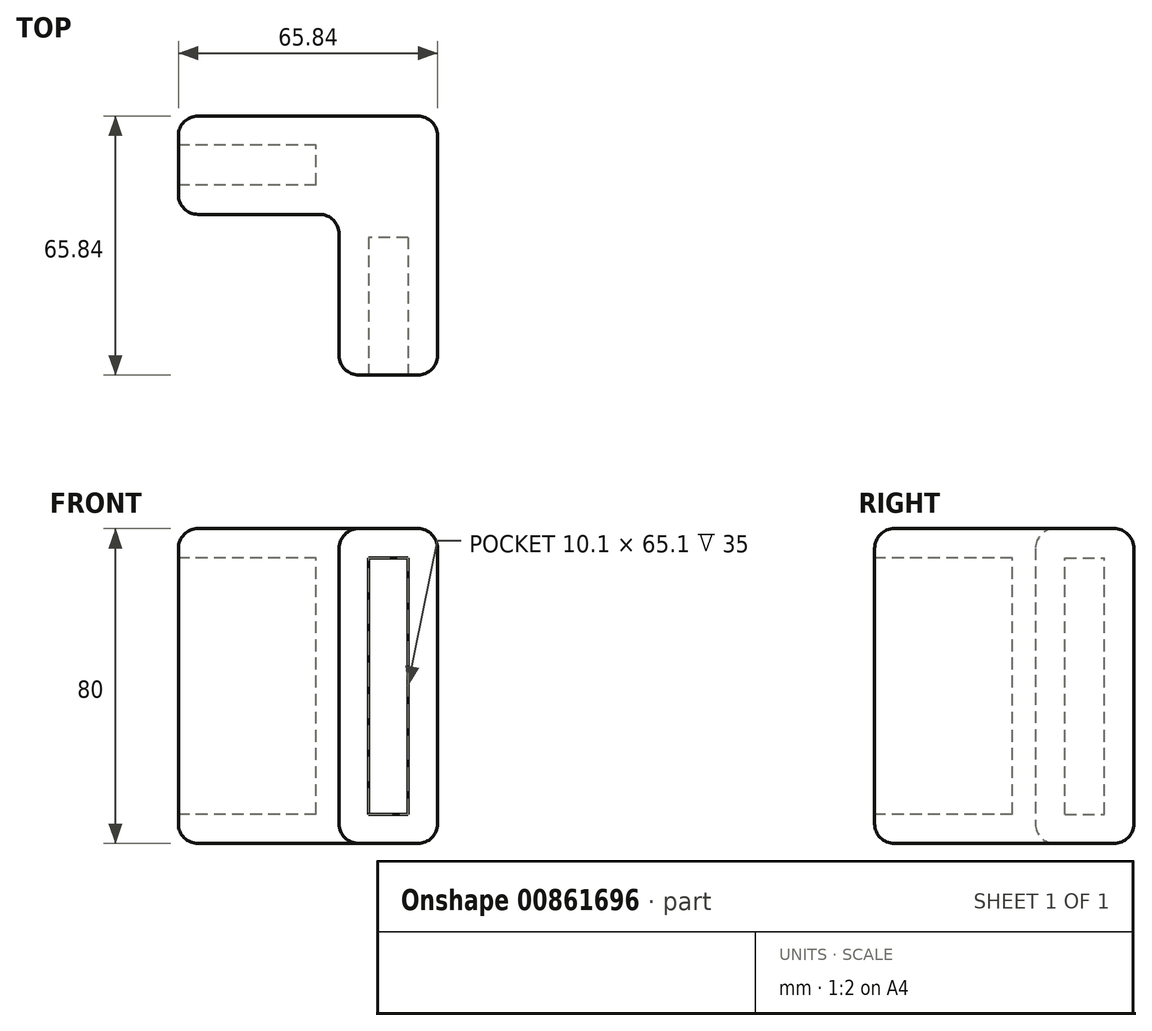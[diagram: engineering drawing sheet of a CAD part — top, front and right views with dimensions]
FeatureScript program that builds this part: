
annotation { "Feature Type Name" : "Feature", "Feature Type Description" : "" }
export const myFeature = defineFeature(function(context is Context, id is Id, definition is map)
    precondition{}
    {
        {
            var Q0;
            Q0=qCreatedBy(makeId("Top.planeOp"),FACE);
            var sketch = newSketch(context, id + "F0", { "sketchPlane" : qUnion([Q0])});
            skLineSegment(sketch, "E0", {"start": v(0, 0) * mm, "end": v(35.84, 0) * mm});
            skLineSegment(sketch, "E1", {"start": v(40.84, -5) * mm, "end": v(40.84, -40.84) * mm});
            skLineSegment(sketch, "E2", {"start": v(40.84, -40.84) * mm, "end": v(48.29, -40.84) * mm});
            skLineSegment(sketch, "E3", {"start": v(48.29, -40.84) * mm, "end": v(48.29, -5.84) * mm});
            skLineSegment(sketch, "E4", {"start": v(48.29, -5.84) * mm, "end": v(58.39, -5.84) * mm});
            skLineSegment(sketch, "E5", {"start": v(58.39, -5.84) * mm, "end": v(58.39, -40.84) * mm});
            skLineSegment(sketch, "E6", {"start": v(58.39, -40.84) * mm, "end": v(65.84, -40.84) * mm});
            skLineSegment(sketch, "E7", {"start": v(65.84, -40.84) * mm, "end": v(65.84, 20) * mm});
            skLineSegment(sketch, "E8", {"start": v(60.84, 25) * mm, "end": v(0, 25) * mm});
            skLineSegment(sketch, "E9", {"start": v(0, 25) * mm, "end": v(0, 17.55) * mm});
            skLineSegment(sketch, "E10", {"start": v(0, 17.55) * mm, "end": v(35, 17.55) * mm});
            skLineSegment(sketch, "E11", {"start": v(35, 17.55) * mm, "end": v(35, 7.45) * mm});
            skLineSegment(sketch, "E12", {"start": v(35, 7.45) * mm, "end": v(0, 7.45) * mm});
            skLineSegment(sketch, "E13", {"start": v(0, 7.45) * mm, "end": v(0, 0) * mm});
            skPoint(sketch, "E14.visualSharp", {"position": v(65.84, 25) * mm});
            skArc(sketch, "E14.filletArc", {"start": v(65.84, 20) * mm, "mid": v(64.37, 23.54) * mm, "end": v(60.84, 25) * mm});
            skPoint(sketch, "E15.visualSharp", {"position": v(40.84, 0) * mm});
            skArc(sketch, "E15.filletArc", {"start": v(40.84, -5) * mm, "mid": v(39.37, -1.46) * mm, "end": v(35.84, 0) * mm});
            skLineSegment(sketch, "E16", {"start": v(48.29, -40.84) * mm, "end": v(58.39, -40.84) * mm});
            skLineSegment(sketch, "E17", {"start": v(0, 17.55) * mm, "end": v(0, 7.45) * mm});
            skSolve(sketch);
        }
        {
            var Q0;
            Q0=makeQuery(id+"F0.imprint","IMPRINT",FACE,{"disambiguationData":[TD([[makeQuery(id+"F0.imprint","IMPRINT",EDGE,{"derivedFrom":sQuery(id+"F0.wireOp",EDGE,"E0")}),1.0]])]});
            var Q1;
            Q1=makeQuery(id+"F0.imprint","IMPRINT",FACE,{"disambiguationData":[TD([[makeQuery(id+"F0.imprint","IMPRINT",EDGE,{"derivedFrom":sQuery(id+"F0.wireOp",EDGE,"E10")}),-1.0]])]});
            var Q2;
            Q2=makeQuery(id+"F0.imprint","IMPRINT",FACE,{"disambiguationData":[TD([[makeQuery(id+"F0.imprint","IMPRINT",EDGE,{"derivedFrom":sQuery(id+"F0.wireOp",EDGE,"E3")}),-1.0]])]});
            extrude(context, id + "F1", {"entities" : qUnion([Q0, Q1, Q2]), "depth" : 80 * mm, "offsetDistance" : 25 * mm});
        }
        {
            var Q0;
            Q0=makeQuery(id+"F1.opExtrude","SWEPT_FACE",FACE,{"disambiguationData":[OSD([sQuery(id+"F0.wireOp",EDGE,"E9"),sQuery(id+"F0.wireOp",EDGE,"E13"),sQuery(id+"F0.wireOp",EDGE,"E17")])]});
            var sketch = newSketch(context, id + "F2", { "sketchPlane" : qUnion([Q0])});
            skLineSegment(sketch, "E18.0", {"start": v(-25, 80) * mm, "end": v(-25, 0) * mm});
            skPoint(sketch, "E19.0", {"position": v(-12.5, 80) * mm});
            skPoint(sketch, "E20.0", {"position": v(0, 40) * mm});
            skPoint(sketch, "E21.0", {"position": v(-12.5, 0) * mm});
            skLineSegment(sketch, "E22.bottom", {"start": v(-7.45, 7.45) * mm, "end": v(-17.55, 7.45) * mm});
            skLineSegment(sketch, "E22.top", {"start": v(-7.45, 72.55) * mm, "end": v(-17.55, 72.55) * mm});
            skLineSegment(sketch, "E22.left", {"start": v(-7.45, 7.45) * mm, "end": v(-7.45, 72.55) * mm});
            skLineSegment(sketch, "E22.right", {"start": v(-17.55, 7.45) * mm, "end": v(-17.55, 72.55) * mm});
            skPoint(sketch, "E22.middle", {"position": v(-12.5, 40) * mm});
            skSolve(sketch);
        }
        {
            var Q0;
            Q0=makeQuery(id+"F1.opExtrude","SWEPT_FACE",FACE,{"disambiguationData":[OSD([sQuery(id+"F0.wireOp",EDGE,"E2"),sQuery(id+"F0.wireOp",EDGE,"E6"),sQuery(id+"F0.wireOp",EDGE,"E16")])]});
            var sketch = newSketch(context, id + "F3", { "sketchPlane" : qUnion([Q0])});
            skLineSegment(sketch, "E23.0.0", {"start": v(40.84, 0) * mm, "end": v(65.84, 0) * mm});
            skLineSegment(sketch, "E23.0.1", {"start": v(65.84, 0) * mm, "end": v(65.84, 80) * mm});
            skLineSegment(sketch, "E23.0.2", {"start": v(65.84, 80) * mm, "end": v(40.84, 80) * mm});
            skLineSegment(sketch, "E23.0.3", {"start": v(40.84, 80) * mm, "end": v(40.84, 0) * mm});
            skLineSegment(sketch, "E24.bottom", {"start": v(58.39, 7.45) * mm, "end": v(48.29, 7.45) * mm});
            skLineSegment(sketch, "E24.top", {"start": v(58.39, 72.55) * mm, "end": v(48.29, 72.55) * mm});
            skLineSegment(sketch, "E24.left", {"start": v(58.39, 7.45) * mm, "end": v(58.39, 72.55) * mm});
            skLineSegment(sketch, "E24.right", {"start": v(48.29, 7.45) * mm, "end": v(48.29, 72.55) * mm});
            skPoint(sketch, "E24.middle", {"position": v(53.34, 40) * mm});
            skPoint(sketch, "E24.middle.positionSnap0", {"position": v(65.84, 40) * mm});
            skPoint(sketch, "E24.middle.positionSnap1", {"position": v(53.34, 80) * mm});
            skPoint(sketch, "E24.centerSnap0", {"position": v(65.84, 40) * mm});
            skPoint(sketch, "E24.centerSnap1", {"position": v(53.34, 80) * mm});
            skSolve(sketch);
        }
        {
            var Q0;
            Q0=makeQuery(id+"F3.imprint","IMPRINT",FACE,{"disambiguationData":[TD([[makeQuery(id+"F3.imprint","IMPRINT",EDGE,{"derivedFrom":sQuery(id+"F3.wireOp",EDGE,"E24.bottom")}),-1.0]])]});
            extrude(context, id + "F4", {"entities" : qUnion([Q0]), "operationType" : NewBodyOperationType.REMOVE, "oppositeDirection" : true, "depth" : 35 * mm, "offsetDistance" : 25 * mm});
        }
        {
            var Q0;
            Q0=makeQuery(id+"F2.imprint","IMPRINT",FACE,{"disambiguationData":[TD([[makeQuery(id+"F2.imprint","IMPRINT",EDGE,{"derivedFrom":sQuery(id+"F2.wireOp",EDGE,"E22.bottom")}),-1.0]])]});
            extrude(context, id + "F5", {"entities" : qUnion([Q0]), "operationType" : NewBodyOperationType.REMOVE, "oppositeDirection" : true, "depth" : 35 * mm, "offsetDistance" : 25 * mm});
        }
        {
            var Q0;
            Q0=makeQuery(id+"F1.opExtrude","CAP_FACE",FACE,{"disambiguationData":[OSD([sQuery(id+"F0.wireOp",EDGE,"E0"),sQuery(id+"F0.wireOp",EDGE,"E1"),sQuery(id+"F0.wireOp",EDGE,"E2"),sQuery(id+"F0.wireOp",EDGE,"E6"),sQuery(id+"F0.wireOp",EDGE,"E7"),sQuery(id+"F0.wireOp",EDGE,"E8"),sQuery(id+"F0.wireOp",EDGE,"E9"),sQuery(id+"F0.wireOp",EDGE,"E13"),sQuery(id+"F0.wireOp",EDGE,"E14.filletArc"),sQuery(id+"F0.wireOp",EDGE,"E15.filletArc"),sQuery(id+"F0.wireOp",EDGE,"E16"),sQuery(id+"F0.wireOp",EDGE,"E17")])],"isStart":false});
            var Q1;
            Q1=makeQuery(id+"F1.opExtrude","CAP_FACE",FACE,{"disambiguationData":[OSD([sQuery(id+"F0.wireOp",EDGE,"E0"),sQuery(id+"F0.wireOp",EDGE,"E1"),sQuery(id+"F0.wireOp",EDGE,"E2"),sQuery(id+"F0.wireOp",EDGE,"E6"),sQuery(id+"F0.wireOp",EDGE,"E7"),sQuery(id+"F0.wireOp",EDGE,"E8"),sQuery(id+"F0.wireOp",EDGE,"E9"),sQuery(id+"F0.wireOp",EDGE,"E13"),sQuery(id+"F0.wireOp",EDGE,"E14.filletArc"),sQuery(id+"F0.wireOp",EDGE,"E15.filletArc"),sQuery(id+"F0.wireOp",EDGE,"E16"),sQuery(id+"F0.wireOp",EDGE,"E17")])],"isStart":true});
            var Q2;
            Q2=makeQuery(id+"F1.opExtrude","SWEPT_EDGE",EDGE,{"disambiguationData":[OSD([sQuery(id+"F0.wireOp",EDGE,"E6"),sQuery(id+"F0.wireOp",EDGE,"E7")])]});
            var Q3;
            Q3=makeQuery(id+"F1.opExtrude","SWEPT_EDGE",EDGE,{"disambiguationData":[OSD([sQuery(id+"F0.wireOp",EDGE,"E1"),sQuery(id+"F0.wireOp",EDGE,"E2")])]});
            var Q4;
            Q4=makeQuery(id+"F1.opExtrude","SWEPT_EDGE",EDGE,{"disambiguationData":[OSD([sQuery(id+"F0.wireOp",EDGE,"E0"),sQuery(id+"F0.wireOp",EDGE,"E13")])]});
            var Q5;
            Q5=makeQuery(id+"F1.opExtrude","SWEPT_EDGE",EDGE,{"disambiguationData":[OSD([sQuery(id+"F0.wireOp",EDGE,"E8"),sQuery(id+"F0.wireOp",EDGE,"E9")])]});
            fillet(context, id + "F6", {"entities" : qUnion([Q0, Q1, Q2, Q3, Q4, Q5]), "radius" : 5 * mm, "tangentPropagation" : true, "allowEdgeOverflow" : false});
        }
    });
